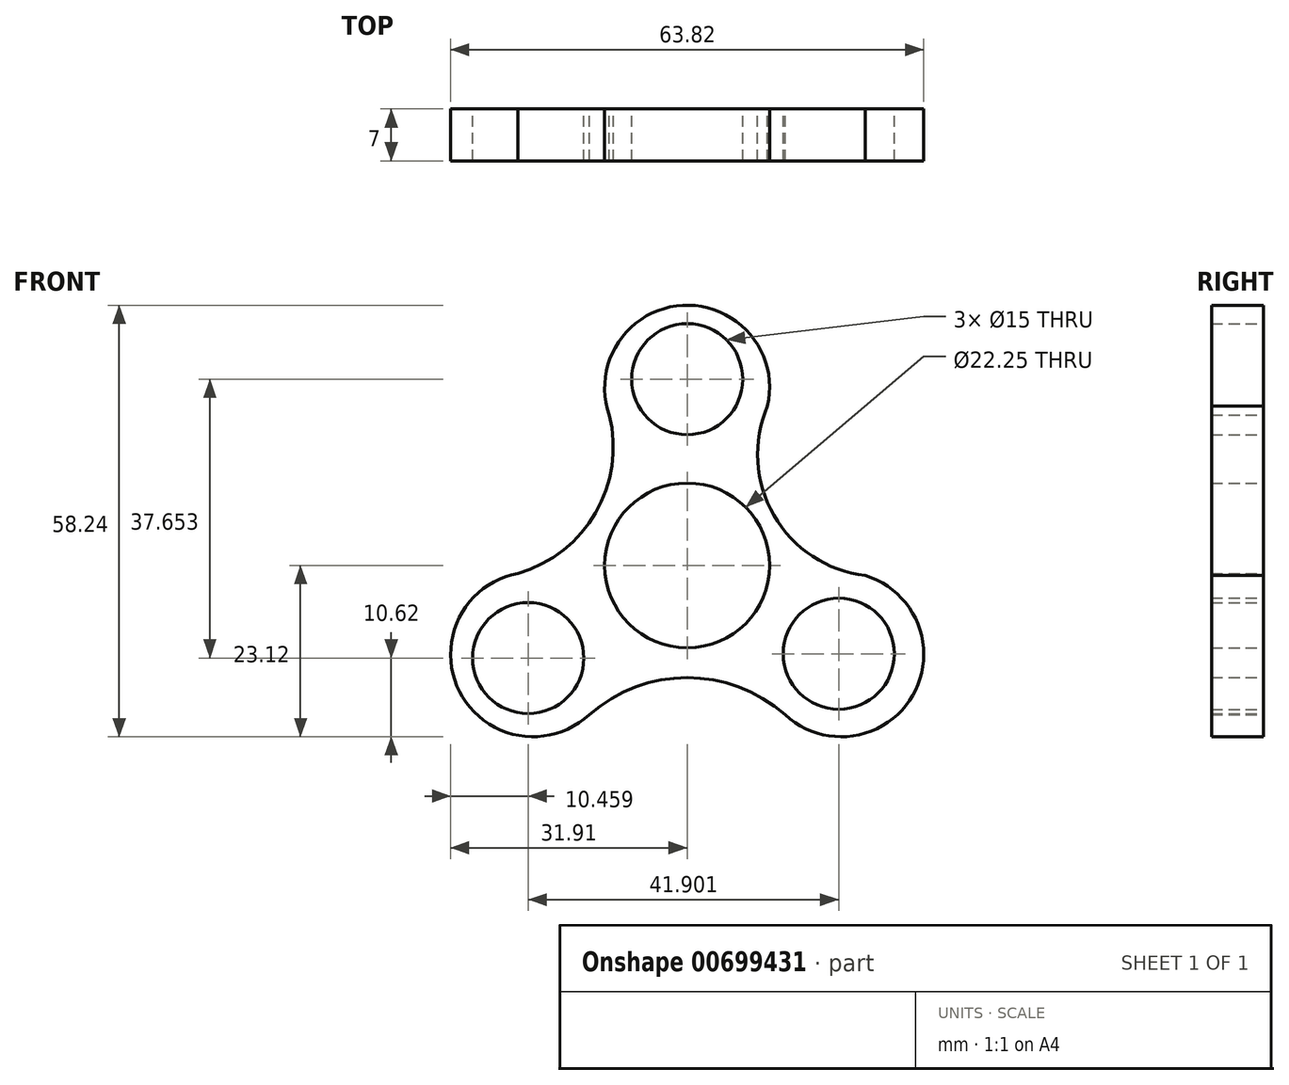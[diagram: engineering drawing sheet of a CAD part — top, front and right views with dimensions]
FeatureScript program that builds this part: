
annotation { "Feature Type Name" : "Feature", "Feature Type Description" : "" }
export const myFeature = defineFeature(function(context is Context, id is Id, definition is map)
    precondition{}
    {
        {
            var Q0;
            Q0=qCreatedBy(makeId("Front.planeOp"),FACE);
            var sketch = newSketch(context, id + "F0", { "sketchPlane" : qUnion([Q0])});
            skCircle(sketch, "E0", {"center": v(0, 0) * mm, "radius": 11.12 * mm});
            skArc(sketch, "E1", {"start": v(10.84, 21.51) * mm, "mid": v(-0.62, 35.1) * mm, "end": v(-10.5, 20.32) * mm});
            skArc(sketch, "E2", {"start": v(-22.85, -1.07) * mm, "mid": v(-30.71, -17.02) * mm, "end": v(-13.2, -20.15) * mm});
            skArc(sketch, "E3", {"start": v(13.2, -20.15) * mm, "mid": v(30.42, -17.56) * mm, "end": v(24.05, -1.36) * mm});
            skLineSegment(sketch, "E4", {"start": v(0, 0) * mm, "end": v(-41.57, -24) * mm});
            skLineSegment(sketch, "E5", {"start": v(0, 0) * mm, "end": v(41.57, -24) * mm});
            skLineSegment(sketch, "E6", {"start": v(0, 0) * mm, "end": v(0, 65.6) * mm});
            skArc(sketch, "E7", {"start": v(-24.05, -1.36) * mm, "mid": v(-12.34, 7.12) * mm, "end": v(-10.84, 21.51) * mm});
            skArc(sketch, "E8", {"start": v(10.84, 21.51) * mm, "mid": v(11.7, 6.75) * mm, "end": v(24.05, -1.36) * mm});
            skArc(sketch, "E9", {"start": v(13.2, -20.15) * mm, "mid": v(0, -15.15) * mm, "end": v(-13.2, -20.15) * mm});
            skSolve(sketch);
        }
        {
            var Q0;
            Q0 = qSketchRegion(id + "F0", true);
            extrude(context, id + "F1", {"entities" : qUnion([Q0]), "depth" : 7 * mm, "offsetDistance" : 25 * mm});
        }
        {
            var Q0;
            Q0=qCreatedBy(makeId("Front.planeOp"),FACE);
            var sketch = newSketch(context, id + "F2", { "sketchPlane" : qUnion([Q0])});
            skCircle(sketch, "E10", {"center": v(20.45, -11.92) * mm, "radius": 7.5 * mm});
            skCircle(sketch, "E11", {"center": v(-21.45, -12.5) * mm, "radius": 7.5 * mm});
            skCircle(sketch, "E12", {"center": v(0, 25.15) * mm, "radius": 7.5 * mm});
            skSolve(sketch);
        }
        {
            var Q0;
            Q0 = qSketchRegion(id + "F2", true);
            extrude(context, id + "F3", {"entities" : qUnion([Q0]), "operationType" : NewBodyOperationType.REMOVE, "depth" : 47.6 * mm, "offsetDistance" : 25 * mm});
        }
    });
